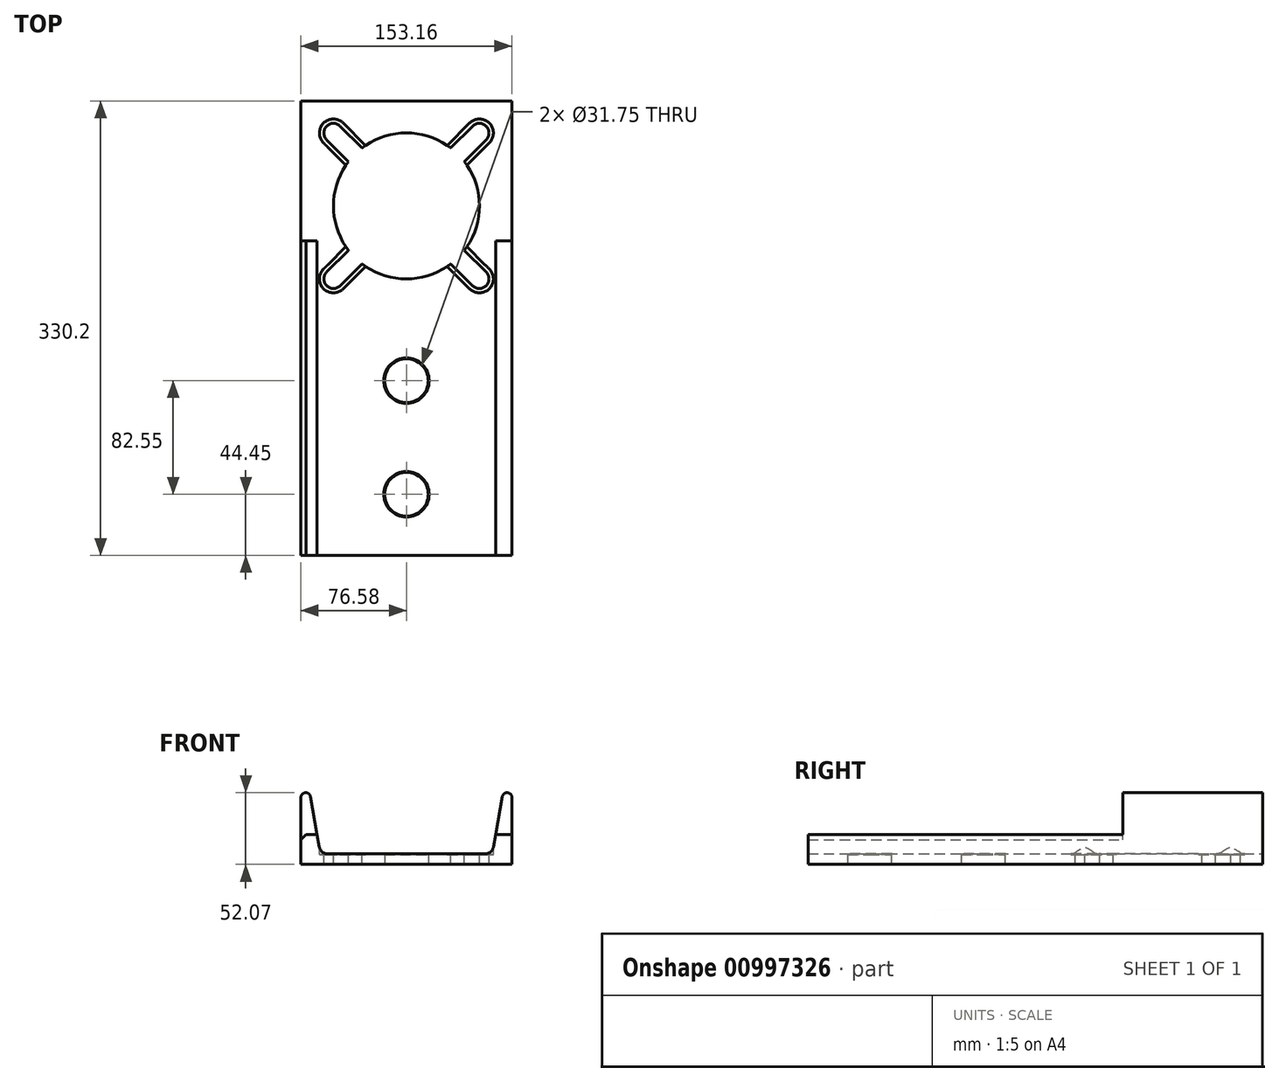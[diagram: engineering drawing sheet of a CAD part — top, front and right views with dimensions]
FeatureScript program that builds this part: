
annotation { "Feature Type Name" : "Feature", "Feature Type Description" : "" }
export const myFeature = defineFeature(function(context is Context, id is Id, definition is map)
    precondition{}
    {
        {
            var Q0;
            Q0=qCreatedBy(makeId("Front.planeOp"),FACE);
            var sketch = newSketch(context, id + "F0", { "sketchPlane" : qUnion([Q0])});
            skLineSegment(sketch, "E0.bottom", {"start": v(-76.58, 0) * mm, "end": v(76.58, 0) * mm});
            skLineSegment(sketch, "E0.top", {"start": v(-73.4, 52.07) * mm, "end": v(-72.9, 52.07) * mm});
            skLineSegment(sketch, "E0.left", {"start": v(-76.58, 0) * mm, "end": v(-76.58, 48.9) * mm});
            skLineSegment(sketch, "E0.right", {"start": v(76.58, 0) * mm, "end": v(76.58, 52.07) * mm});
            skLineSegment(sketch, "E1", {"start": v(-69.77, 49.45) * mm, "end": v(-63.32, 12.87) * mm});
            skLineSegment(sketch, "E2", {"start": v(-57.06, 7.62) * mm, "end": v(0, 7.62) * mm});
            skPoint(sketch, "E3.newPointA", {"position": v(-76.58, 7.62) * mm});
            skArc(sketch, "E3.filletArc", {"start": v(-63.32, 12.87) * mm, "mid": v(-61.15, 9.1) * mm, "end": v(-57.06, 7.62) * mm});
            skPoint(sketch, "E4.visualSharp", {"position": v(-76.58, 52.07) * mm});
            skArc(sketch, "E4.filletArc", {"start": v(-73.4, 52.07) * mm, "mid": v(-75.65, 51.14) * mm, "end": v(-76.58, 48.9) * mm});
            skPoint(sketch, "E5.visualSharp", {"position": v(-70.23, 52.07) * mm});
            skArc(sketch, "E5.filletArc", {"start": v(-69.77, 49.45) * mm, "mid": v(-70.85, 51.33) * mm, "end": v(-72.9, 52.07) * mm});
            skArc(sketch, "E6.MirrorCS", {"start": v(73.4, 52.07) * mm, "mid": v(75.65, 51.14) * mm, "end": v(76.58, 48.9) * mm});
            skLineSegment(sketch, "E7.MirrorCS", {"start": v(73.4, 52.07) * mm, "end": v(72.9, 52.07) * mm});
            skArc(sketch, "E8.MirrorCS", {"start": v(69.77, 49.45) * mm, "mid": v(70.85, 51.33) * mm, "end": v(72.9, 52.07) * mm});
            skLineSegment(sketch, "E9.MirrorCS", {"start": v(69.77, 49.45) * mm, "end": v(63.32, 12.87) * mm});
            skPoint(sketch, "E10.MirrorP", {"position": v(76.58, 7.62) * mm});
            skLineSegment(sketch, "E11.MirrorCS", {"start": v(57.06, 7.62) * mm, "end": v(0, 7.62) * mm});
            skArc(sketch, "E12.MirrorCS", {"start": v(63.32, 12.87) * mm, "mid": v(61.15, 9.1) * mm, "end": v(57.06, 7.62) * mm});
            skPoint(sketch, "E13.MirrorP", {"position": v(76.58, 52.07) * mm});
            skLineSegment(sketch, "E14.MirrorCS", {"start": v(76.58, 0) * mm, "end": v(76.58, 48.9) * mm});
            skPoint(sketch, "E15.MirrorP", {"position": v(70.23, 52.07) * mm});
            skSolve(sketch);
        }
        {
            var Q0;
            Q0 = qSketchRegion(id + "F0", true);
            extrude(context, id + "F1", {"entities" : qUnion([Q0]), "depth" : 330.2 * mm, "offsetDistance" : 25.4 * mm});
        }
        {
            var Q0;
            Q0=makeQuery(id+"F1.opExtrude","CAP_FACE",FACE,{"disambiguationData":[OSD([sQuery(id+"F0.wireOp",EDGE,"E0.bottom"),sQuery(id+"F0.wireOp",EDGE,"E0.top"),sQuery(id+"F0.wireOp",EDGE,"E0.left"),sQuery(id+"F0.wireOp",EDGE,"E1"),sQuery(id+"F0.wireOp",EDGE,"E2"),sQuery(id+"F0.wireOp",EDGE,"E3.filletArc"),sQuery(id+"F0.wireOp",EDGE,"E4.filletArc"),sQuery(id+"F0.wireOp",EDGE,"E5.filletArc"),sQuery(id+"F0.wireOp",EDGE,"E6.MirrorCS"),sQuery(id+"F0.wireOp",EDGE,"E7.MirrorCS"),sQuery(id+"F0.wireOp",EDGE,"E8.MirrorCS"),sQuery(id+"F0.wireOp",EDGE,"E9.MirrorCS"),sQuery(id+"F0.wireOp",EDGE,"E11.MirrorCS"),sQuery(id+"F0.wireOp",EDGE,"E12.MirrorCS"),sQuery(id+"F0.wireOp",EDGE,"E14.MirrorCS")])],"isStart":false});
            var sketch = newSketch(context, id + "F2", { "sketchPlane" : qUnion([Q0])});
            skLineSegment(sketch, "E16.bottom", {"start": v(-82.55, 57.15) * mm, "end": v(82.55, 57.15) * mm});
            skLineSegment(sketch, "E16.top", {"start": v(-82.55, 21.59) * mm, "end": v(82.55, 21.6) * mm});
            skLineSegment(sketch, "E16.left", {"start": v(-82.55, 57.15) * mm, "end": v(-82.55, 21.59) * mm});
            skLineSegment(sketch, "E16.right", {"start": v(82.55, 57.15) * mm, "end": v(82.55, 21.6) * mm});
            skSolve(sketch);
        }
        {
            var Q0;
            Q0 = qSketchRegion(id + "F2", true);
            extrude(context, id + "F3", {"entities" : qUnion([Q0]), "operationType" : NewBodyOperationType.REMOVE, "oppositeDirection" : true, "depth" : 228.6 * mm, "offsetDistance" : 25.4 * mm});
        }
        {
            var Q0;
            Q0=makeQuery(id+"F3.boolean.opBoolean","INTERSECT",EDGE,{"derivedFrom":[makeQuery(id+"F1.opExtrude","SWEPT_FACE",FACE,{"disambiguationData":[OSD([sQuery(id+"F0.wireOp",EDGE,"E14.MirrorCS")])]}),makeQuery(id+"F3.opExtrude","SWEPT_FACE",FACE,{"disambiguationData":[OSD([sQuery(id+"F2.wireOp",EDGE,"E16.top")])]})]});
            var Q1;
            Q1=makeQuery(id+"F3.boolean.opBoolean","INTERSECT",EDGE,{"derivedFrom":[makeQuery(id+"F1.opExtrude","SWEPT_FACE",FACE,{"disambiguationData":[OSD([sQuery(id+"F0.wireOp",EDGE,"E0.left")])]}),makeQuery(id+"F3.opExtrude","SWEPT_FACE",FACE,{"disambiguationData":[OSD([sQuery(id+"F2.wireOp",EDGE,"E16.top")])]})]});
            chamfer(context, id + "F4", {"entities" : qUnion([Q0, Q1]), "width" : 3.8 * mm, "tangentPropagation" : true});
        }
        {
            var Q0;
            Q0=makeQuery(id+"F1.opExtrude","SWEPT_FACE",FACE,{"disambiguationData":[OSD([sQuery(id+"F0.wireOp",EDGE,"E2"),sQuery(id+"F0.wireOp",EDGE,"E11.MirrorCS")])]});
            var sketch = newSketch(context, id + "F5", { "sketchPlane" : qUnion([Q0])});
            skArc(sketch, "E17", {"start": v(-42.1, -43.97) * mm, "mid": v(-53.02, -76.2) * mm, "end": v(-42.1, -108.43) * mm});
            skArc(sketch, "E18", {"start": v(-48.08, -18.25) * mm, "mid": v(-57.95, -18.25) * mm, "end": v(-57.95, -28.12) * mm});
            skLineSegment(sketch, "E19", {"start": v(0, -76.2) * mm, "end": v(-53.01, -23.19) * mm, "construction": true});
            skLineSegment(sketch, "E20", {"start": v(-32.23, -34.1) * mm, "end": v(-48.08, -18.25) * mm});
            skLineSegment(sketch, "E21", {"start": v(-42.1, -43.97) * mm, "end": v(-57.95, -28.12) * mm});
            skLineSegment(sketch, "E22.1.0", {"start": v(-42.1, -108.43) * mm, "end": v(-57.95, -124.28) * mm});
            skLineSegment(sketch, "E22.1.1", {"start": v(-32.23, -118.3) * mm, "end": v(-48.08, -134.15) * mm});
            skArc(sketch, "E22.1.2", {"start": v(-57.95, -124.28) * mm, "mid": v(-57.95, -134.15) * mm, "end": v(-48.08, -134.15) * mm});
            skLineSegment(sketch, "E22.2.0", {"start": v(32.23, -118.3) * mm, "end": v(48.08, -134.15) * mm});
            skLineSegment(sketch, "E22.2.1", {"start": v(42.1, -108.43) * mm, "end": v(57.95, -124.28) * mm});
            skArc(sketch, "E22.2.2", {"start": v(48.08, -134.15) * mm, "mid": v(57.95, -134.15) * mm, "end": v(57.95, -124.28) * mm});
            skLineSegment(sketch, "E22.3.0", {"start": v(42.1, -43.97) * mm, "end": v(57.95, -28.12) * mm});
            skLineSegment(sketch, "E22.3.1", {"start": v(32.23, -34.1) * mm, "end": v(48.08, -18.25) * mm});
            skArc(sketch, "E22.3.2", {"start": v(57.95, -28.12) * mm, "mid": v(57.95, -18.25) * mm, "end": v(48.08, -18.25) * mm});
            skArc(sketch, "E23.trimOffspring", {"start": v(-32.23, -118.3) * mm, "mid": v(0, -129.22) * mm, "end": v(32.23, -118.3) * mm});
            skArc(sketch, "E24.trimOffspring", {"start": v(42.1, -108.43) * mm, "mid": v(53.02, -76.2) * mm, "end": v(42.1, -43.97) * mm});
            skArc(sketch, "E25.trimOffspring", {"start": v(32.23, -34.1) * mm, "mid": v(0, -23.18) * mm, "end": v(-32.23, -34.1) * mm});
            skSolve(sketch);
        }
        {
            var Q0;
            Q0 = qSketchRegion(id + "F5", true);
            extrude(context, id + "F6", {"entities" : qUnion([Q0]), "operationType" : NewBodyOperationType.REMOVE, "oppositeDirection" : true, "depth" : 25.4 * mm, "offsetDistance" : 25.4 * mm});
        }
        {
            var Q0;
            {var subQ0=sQuery(id+"F5.wireOp",EDGE,"E22.1.1");var subQ3=sQuery(id+"F0.wireOp",EDGE,"E11.MirrorCS");var subQ4=sQuery(id+"F0.wireOp",EDGE,"E2");Q0=makeQuery(id+"F6.boolean.opBoolean","SPLIT",FACE,{"disambiguationData":[TD([makeQuery(id+"F6.opExtrude","SWEPT_FACE",FACE,{"disambiguationData":[OSD([subQ0])]})])],"derivedFrom":makeQuery(id+"F1.opExtrude","SWEPT_FACE",FACE,{"disambiguationData":[OSD([subQ4,subQ3])]})});}
            var sketch = newSketch(context, id + "F7", { "sketchPlane" : qUnion([Q0])});
            skCircle(sketch, "E26", {"center": v(-53.01, -23.19) * mm, "radius": 10.16 * mm});
            skCircle(sketch, "E27.1.0", {"center": v(-53.01, -129.21) * mm, "radius": 10.16 * mm});
            skCircle(sketch, "E27.2.0", {"center": v(53.01, -129.21) * mm, "radius": 10.16 * mm});
            skCircle(sketch, "E27.3.0", {"center": v(53.01, -23.19) * mm, "radius": 10.16 * mm});
            skPoint(sketch, "E27.center", {"position": v(0, -76.2) * mm});
            skLineSegment(sketch, "E28", {"start": v(0, -76.2) * mm, "end": v(-53.01, -23.19) * mm, "construction": true});
            skLineSegment(sketch, "E29", {"start": v(-43.13, -47.43) * mm, "end": v(-60.2, -30.37) * mm});
            skLineSegment(sketch, "E30", {"start": v(-28.77, -33.06) * mm, "end": v(-45.83, -16) * mm});
            skLineSegment(sketch, "E31", {"start": v(-43.13, -47.43) * mm, "end": v(-28.77, -33.06) * mm});
            skLineSegment(sketch, "E32.1.0", {"start": v(-28.77, -119.33) * mm, "end": v(-45.83, -136.4) * mm});
            skLineSegment(sketch, "E32.1.1", {"start": v(-28.77, -119.33) * mm, "end": v(-43.14, -104.97) * mm});
            skLineSegment(sketch, "E32.1.2", {"start": v(-43.14, -104.97) * mm, "end": v(-60.2, -122.03) * mm});
            skLineSegment(sketch, "E32.2.0", {"start": v(43.13, -104.97) * mm, "end": v(60.2, -122.03) * mm});
            skLineSegment(sketch, "E32.2.1", {"start": v(43.13, -104.97) * mm, "end": v(28.77, -119.34) * mm});
            skLineSegment(sketch, "E32.2.2", {"start": v(28.77, -119.34) * mm, "end": v(45.83, -136.4) * mm});
            skLineSegment(sketch, "E32.3.0", {"start": v(28.77, -33.07) * mm, "end": v(45.83, -16) * mm});
            skLineSegment(sketch, "E32.3.1", {"start": v(28.77, -33.07) * mm, "end": v(43.14, -47.43) * mm});
            skLineSegment(sketch, "E32.3.2", {"start": v(43.14, -47.43) * mm, "end": v(60.2, -30.37) * mm});
            skSolve(sketch);
        }
        {
            var Q0;
            Q0 = qSketchRegion(id + "F7", true);
            extrude(context, id + "F8", {"entities" : qUnion([Q0]), "operationType" : NewBodyOperationType.REMOVE, "oppositeDirection" : true, "depth" : 0.64 * mm, "offsetDistance" : 25.4 * mm});
        }
        {
            var Q0;
            Q0 = qSketchRegion(id + "F7", true);
            extrude(context, id + "F9", {"entities" : qUnion([Q0]), "operationType" : NewBodyOperationType.REMOVE, "depth" : 25.4 * mm, "offsetDistance" : 25.4 * mm});
        }
        {
            var Q0;
            Q0=makeQuery(id+"F1.opExtrude","SWEPT_FACE",FACE,{"disambiguationData":[OSD([sQuery(id+"F0.wireOp",EDGE,"E0.bottom")])]});
            var sketch = newSketch(context, id + "F10", { "sketchPlane" : qUnion([Q0])});
            skCircle(sketch, "E33", {"center": v(0, 285.75) * mm, "radius": 15.88 * mm});
            skCircle(sketch, "E34", {"center": v(0, 203.2) * mm, "radius": 15.88 * mm});
            skSolve(sketch);
        }
        {
            var Q0;
            Q0 = qSketchRegion(id + "F10", true);
            extrude(context, id + "F11", {"entities" : qUnion([Q0]), "operationType" : NewBodyOperationType.REMOVE, "oppositeDirection" : true, "depth" : 25.4 * mm, "offsetDistance" : 25.4 * mm});
        }
        {
            var Q0;
            {var subQ4=sQuery(id+"F5.wireOp",EDGE,"E22.1.1");var subQ7=sQuery(id+"F0.wireOp",EDGE,"E11.MirrorCS");var subQ8=sQuery(id+"F0.wireOp",EDGE,"E2");Q0=makeQuery(id+"F11.boolean.opBoolean","INTERSECT",EDGE,{"derivedFrom":[makeQuery(id+"F6.boolean.opBoolean","SPLIT",FACE,{"disambiguationData":[TD([makeQuery(id+"F6.opExtrude","SWEPT_FACE",FACE,{"disambiguationData":[OSD([subQ4])]})])],"derivedFrom":makeQuery(id+"F1.opExtrude","SWEPT_FACE",FACE,{"disambiguationData":[OSD([subQ8,subQ7])]})}),makeQuery(id+"F11.opExtrude","SWEPT_FACE",FACE,{"disambiguationData":[OSD([sQuery(id+"F10.wireOp",EDGE,"E34")])]})]});}
            var Q1;
            Q1=makeQuery(id+"F11.boolean.opBoolean","COPY",EDGE,{"derivedFrom":makeQuery(id+"F11.opExtrude","CAP_EDGE",EDGE,{"disambiguationData":[OSD([sQuery(id+"F10.wireOp",EDGE,"E34")])],"isStart":true})});
            var Q2;
            Q2=makeQuery(id+"F11.boolean.opBoolean","COPY",EDGE,{"derivedFrom":makeQuery(id+"F11.opExtrude","CAP_EDGE",EDGE,{"disambiguationData":[OSD([sQuery(id+"F10.wireOp",EDGE,"E33")])],"isStart":true})});
            var Q3;
            {var subQ4=sQuery(id+"F5.wireOp",EDGE,"E22.1.1");var subQ7=sQuery(id+"F0.wireOp",EDGE,"E11.MirrorCS");var subQ8=sQuery(id+"F0.wireOp",EDGE,"E2");Q3=makeQuery(id+"F11.boolean.opBoolean","INTERSECT",EDGE,{"derivedFrom":[makeQuery(id+"F6.boolean.opBoolean","SPLIT",FACE,{"disambiguationData":[TD([makeQuery(id+"F6.opExtrude","SWEPT_FACE",FACE,{"disambiguationData":[OSD([subQ4])]})])],"derivedFrom":makeQuery(id+"F1.opExtrude","SWEPT_FACE",FACE,{"disambiguationData":[OSD([subQ8,subQ7])]})}),makeQuery(id+"F11.opExtrude","SWEPT_FACE",FACE,{"disambiguationData":[OSD([sQuery(id+"F10.wireOp",EDGE,"E33")])]})]});}
            chamfer(context, id + "F12", {"entities" : qUnion([Q0, Q1, Q2, Q3]), "width" : 0.64 * mm, "tangentPropagation" : true});
        }
    });
